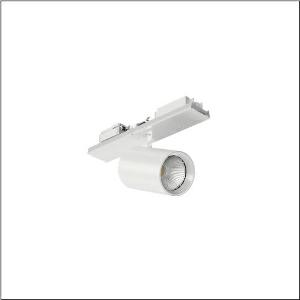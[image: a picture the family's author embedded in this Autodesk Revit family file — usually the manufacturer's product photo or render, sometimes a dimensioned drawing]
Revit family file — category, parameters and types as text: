
# Revit family: licross_r__spot_31_51sl12da43b_285d
name_source: partatom
category: Lighting Fixtures
units: mm (PartAtom-declared; Revit-internal decimal feet)

## family parameters
Cut with Voids When Loaded = No
Host = Face
Light Source = No
Part Type = Normal
Room Calculation Point = No
Round Connector Dimension = Use Diameter
Shared = No

## types (1)
- --- (1 x LED, 3650 lm, 28.6 W, 4000K)
    Apparent Load = 29 VA
    CIE Flux Codes = 93 97 99 100 100
    Color Rendering = 90
    Color Temperature = 4000K
    Default Elevation = 1800 mm
    Description = Licross® Spot 31, directional spotlight, light control with lens, of plastic, LED rated luminous flux: 3.650lm, light colour: 940, with plug, 5-pole, mains connection: 220..240V, AC, 50/60Hz, of aluminium, traffic white (RAL 9016), length: 140mm, diameter: 90mm, protection rating (complete): IP20, insulation class (complete): insulation class I (protective earthing), certification: CE, packaging unit: 1 piece
    Height = 175 mm
    Lamp = 1 x LED
    Lamp Light Flux = 3650 lm
    Lamp Power = 28.6 W
    Lamp count = 1
    Length = 90 mm
    Luminous efficacy = 128 lm/W
    Manufacturer = Siteco
    ModVariant = No
    Model = 51SL12DA43B
    Mounting Place = Ceiling
    Mounting Type = Pendant
    Number of Poles = 1
    OnlyDefault = Yes
    Power Factor = 1
    Product Name = Licross® Spot 31
    Product group = directional spotlight
    ProductGroupID = 905
    Protection Class = Protection class I
    Protection Degree = IP 20
    RLX_Detail_Level = 1
    RLX_Emergency_Light_Flux = 0 lm
    RLX_Emergency_Type = 0
    RLX_Emergency_Type_DB = No
    RlxData = <blob elided: 14781 chars, md5=70c61c4f>
    Socket = socket
    Standby Power = 0 W
    System Light Flux = 3650 lm
    System Power = 29 W
    Type Comments = factory setting: luminous flux: 100 % | (ON | ON | ON) | 700 mA
    Type Image = l_1245720.jpg
    URL = http://relux.com
    VarID = @adj_082067
    Voltage = 0 V
    Weight = 0.00 kg
    Width = 0 mm  [stored 0 ft]

note: [stored X ft] marks values corroborated as IEEE doubles in the binary element streams (Revit-internal decimal feet)

## geometry (parser evidence)
native form markers: Sweep x10
no freeform markers — native parametric forms only
